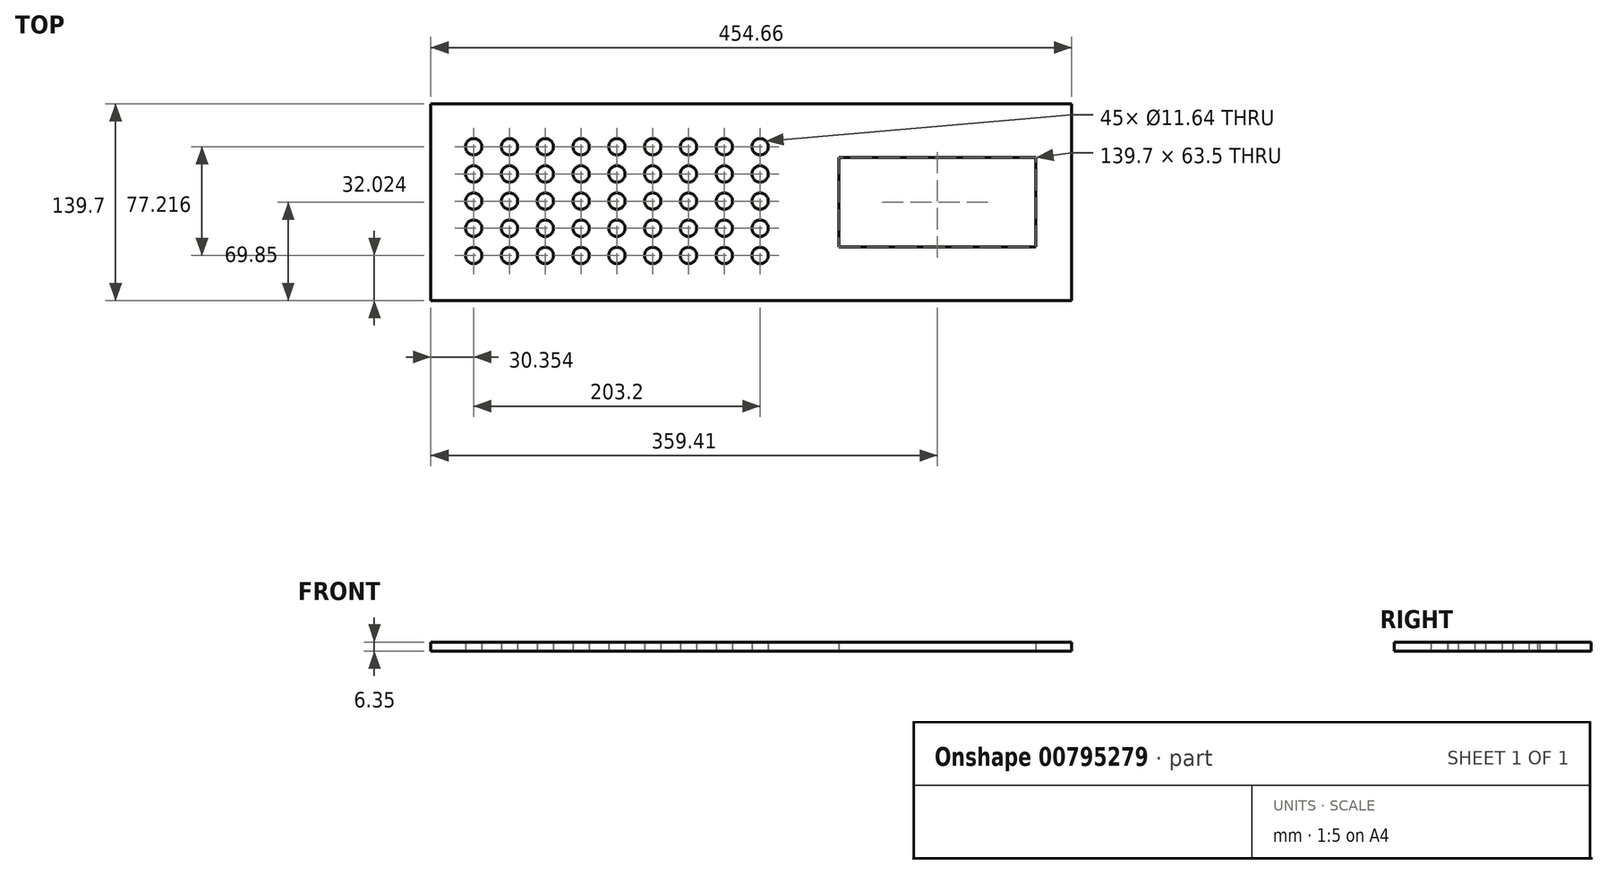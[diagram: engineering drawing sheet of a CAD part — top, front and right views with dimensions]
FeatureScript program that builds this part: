
annotation { "Feature Type Name" : "Feature", "Feature Type Description" : "" }
export const myFeature = defineFeature(function(context is Context, id is Id, definition is map)
    precondition{}
    {
        {
            var Q0;
            Q0=qCreatedBy(makeId("Top.planeOp"),FACE);
            var sketch = newSketch(context, id + "F0", { "sketchPlane" : qUnion([Q0])});
            skLineSegment(sketch, "E0.bottom", {"start": v(227.33, -69.85) * mm, "end": v(-227.33, -69.85) * mm});
            skLineSegment(sketch, "E0.top", {"start": v(227.33, 69.85) * mm, "end": v(-227.33, 69.85) * mm});
            skLineSegment(sketch, "E0.left", {"start": v(227.33, -69.85) * mm, "end": v(227.33, 69.85) * mm});
            skLineSegment(sketch, "E0.right", {"start": v(-227.33, -69.85) * mm, "end": v(-227.33, 69.85) * mm});
            skPoint(sketch, "E0.middle", {"position": v(0, 0) * mm});
            skLineSegment(sketch, "E1.bottom", {"start": v(201.93, -31.75) * mm, "end": v(62.23, -31.75) * mm});
            skLineSegment(sketch, "E1.top", {"start": v(201.93, 31.75) * mm, "end": v(62.23, 31.75) * mm});
            skLineSegment(sketch, "E1.left", {"start": v(201.93, -31.75) * mm, "end": v(201.93, 31.75) * mm});
            skLineSegment(sketch, "E1.right", {"start": v(62.23, -31.75) * mm, "end": v(62.23, 31.75) * mm});
            skPoint(sketch, "E1.middle", {"position": v(132.08, 0) * mm});
            skLineSegment(sketch, "E2", {"start": v(201.93, 31.75) * mm, "end": v(201.93, 69.85) * mm, "construction": true});
            skLineSegment(sketch, "E3", {"start": v(201.93, -31.75) * mm, "end": v(201.93, -69.85) * mm, "construction": true});
            skCircle(sketch, "E4", {"center": v(-196.98, 39.39) * mm, "radius": 5.82 * mm});
            skCircle(sketch, "E5.0.1.0", {"center": v(-196.98, 20.09) * mm, "radius": 5.82 * mm});
            skCircle(sketch, "E5.0.2.0", {"center": v(-196.98, 0.78) * mm, "radius": 5.82 * mm});
            skCircle(sketch, "E5.0.3.0", {"center": v(-196.98, -18.52) * mm, "radius": 5.82 * mm});
            skCircle(sketch, "E5.0.4.0", {"center": v(-196.98, -37.83) * mm, "radius": 5.82 * mm});
            skCircle(sketch, "E5.1.0.0", {"center": v(-171.58, 39.39) * mm, "radius": 5.82 * mm});
            skCircle(sketch, "E5.1.1.0", {"center": v(-171.58, 20.09) * mm, "radius": 5.82 * mm});
            skCircle(sketch, "E5.1.2.0", {"center": v(-171.58, 0.78) * mm, "radius": 5.82 * mm});
            skCircle(sketch, "E5.1.3.0", {"center": v(-171.58, -18.52) * mm, "radius": 5.82 * mm});
            skCircle(sketch, "E5.1.4.0", {"center": v(-171.58, -37.83) * mm, "radius": 5.82 * mm});
            skCircle(sketch, "E5.2.0.0", {"center": v(-146.18, 39.39) * mm, "radius": 5.82 * mm});
            skCircle(sketch, "E5.2.1.0", {"center": v(-146.18, 20.09) * mm, "radius": 5.82 * mm});
            skCircle(sketch, "E5.2.2.0", {"center": v(-146.18, 0.78) * mm, "radius": 5.82 * mm});
            skCircle(sketch, "E5.2.3.0", {"center": v(-146.18, -18.52) * mm, "radius": 5.82 * mm});
            skCircle(sketch, "E5.2.4.0", {"center": v(-146.18, -37.83) * mm, "radius": 5.82 * mm});
            skCircle(sketch, "E5.3.0.0", {"center": v(-120.78, 39.39) * mm, "radius": 5.82 * mm});
            skCircle(sketch, "E5.3.1.0", {"center": v(-120.78, 20.09) * mm, "radius": 5.82 * mm});
            skCircle(sketch, "E5.3.2.0", {"center": v(-120.78, 0.78) * mm, "radius": 5.82 * mm});
            skCircle(sketch, "E5.3.3.0", {"center": v(-120.78, -18.52) * mm, "radius": 5.82 * mm});
            skCircle(sketch, "E5.3.4.0", {"center": v(-120.78, -37.83) * mm, "radius": 5.82 * mm});
            skCircle(sketch, "E5.4.0.0", {"center": v(-95.38, 39.39) * mm, "radius": 5.82 * mm});
            skCircle(sketch, "E5.4.1.0", {"center": v(-95.38, 20.09) * mm, "radius": 5.82 * mm});
            skCircle(sketch, "E5.4.2.0", {"center": v(-95.38, 0.78) * mm, "radius": 5.82 * mm});
            skCircle(sketch, "E5.4.3.0", {"center": v(-95.38, -18.52) * mm, "radius": 5.82 * mm});
            skCircle(sketch, "E5.4.4.0", {"center": v(-95.38, -37.83) * mm, "radius": 5.82 * mm});
            skCircle(sketch, "E5.5.0.0", {"center": v(-69.98, 39.39) * mm, "radius": 5.82 * mm});
            skCircle(sketch, "E5.5.1.0", {"center": v(-69.98, 20.09) * mm, "radius": 5.82 * mm});
            skCircle(sketch, "E5.5.2.0", {"center": v(-69.98, 0.78) * mm, "radius": 5.82 * mm});
            skCircle(sketch, "E5.5.3.0", {"center": v(-69.98, -18.52) * mm, "radius": 5.82 * mm});
            skCircle(sketch, "E5.5.4.0", {"center": v(-69.98, -37.83) * mm, "radius": 5.82 * mm});
            skCircle(sketch, "E5.6.0.0", {"center": v(-44.58, 39.39) * mm, "radius": 5.82 * mm});
            skCircle(sketch, "E5.6.1.0", {"center": v(-44.58, 20.09) * mm, "radius": 5.82 * mm});
            skCircle(sketch, "E5.6.2.0", {"center": v(-44.58, 0.78) * mm, "radius": 5.82 * mm});
            skCircle(sketch, "E5.6.3.0", {"center": v(-44.58, -18.52) * mm, "radius": 5.82 * mm});
            skCircle(sketch, "E5.6.4.0", {"center": v(-44.58, -37.83) * mm, "radius": 5.82 * mm});
            skCircle(sketch, "E5.7.0.0", {"center": v(-19.18, 39.39) * mm, "radius": 5.82 * mm});
            skCircle(sketch, "E5.7.1.0", {"center": v(-19.18, 20.09) * mm, "radius": 5.82 * mm});
            skCircle(sketch, "E5.7.2.0", {"center": v(-19.18, 0.78) * mm, "radius": 5.82 * mm});
            skCircle(sketch, "E5.7.3.0", {"center": v(-19.18, -18.52) * mm, "radius": 5.82 * mm});
            skCircle(sketch, "E5.7.4.0", {"center": v(-19.18, -37.83) * mm, "radius": 5.82 * mm});
            skCircle(sketch, "E5.8.0.0", {"center": v(6.22, 39.39) * mm, "radius": 5.82 * mm});
            skCircle(sketch, "E5.8.1.0", {"center": v(6.22, 20.09) * mm, "radius": 5.82 * mm});
            skCircle(sketch, "E5.8.2.0", {"center": v(6.22, 0.78) * mm, "radius": 5.82 * mm});
            skCircle(sketch, "E5.8.3.0", {"center": v(6.22, -18.52) * mm, "radius": 5.82 * mm});
            skCircle(sketch, "E5.8.4.0", {"center": v(6.22, -37.83) * mm, "radius": 5.82 * mm});
            skLineSegment(sketch, "E5.direction1", {"start": v(-196.98, 39.39) * mm, "end": v(-171.58, 39.39) * mm, "construction": true});
            skLineSegment(sketch, "E5.direction2", {"start": v(-196.98, 39.39) * mm, "end": v(-196.98, 20.09) * mm, "construction": true});
            skSolve(sketch);
        }
        {
            var Q0;
            Q0=makeQuery(id+"F0.imprint","IMPRINT",FACE,{"disambiguationData":[TD([[makeQuery(id+"F0.imprint","IMPRINT",EDGE,{"derivedFrom":sQuery(id+"F0.wireOp",EDGE,"E0.bottom")}),-1.0]])]});
            extrude(context, id + "F1", {"entities" : qUnion([Q0]), "depth" : 6.35 * mm, "offsetDistance" : 25.4 * mm});
        }
    });
